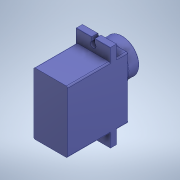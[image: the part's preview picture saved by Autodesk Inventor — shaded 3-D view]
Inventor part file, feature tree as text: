
AUTODESK INVENTOR PART (.ipt)
format: ipt  version: 2021.1 (Build 251245010, 245A)  size: 249,344 bytes
history: imported  units: in
note: dims shown in document units (in); Inventor stores cm internally (conversion verified against a paired STEP export)
features: imported_body x1
ambient origin geometry x8: Origin, YZ Plane, XZ Plane, XY Plane, X Axis, Y Axis, Z Axis, Center Point
bodies: Solid1 (imported_parasolid), Body2 (imported_parasolid)
feature tree (1):
  imported_body  NMx_Import_Brep_tag  [imported B-rep: ~23 faces, bbox_mm=[12.6, 27.2, 22.2]]
